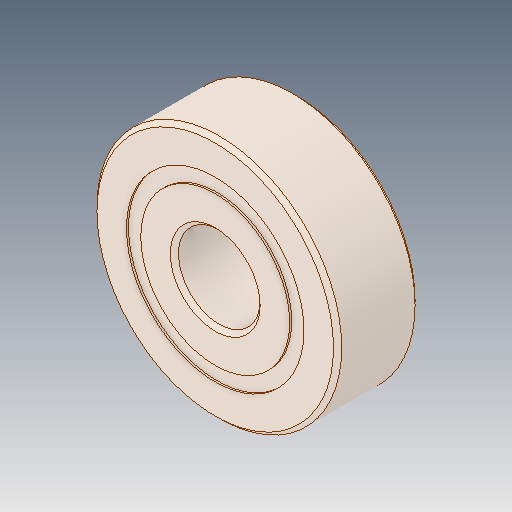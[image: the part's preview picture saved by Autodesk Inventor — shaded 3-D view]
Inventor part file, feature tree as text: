
AUTODESK INVENTOR PART (.ipt)
format: ipt  version: 2019 (Build 230136000, 136)  size: 607,232 bytes
history: native  units: mm
features: other x11, revolve x5
ambient origin geometry x8: Origin, YZ Plane, XZ Plane, XY Plane, X Axis, Y Axis, Z Axis, Center Point
bodies: Solid1 (feature_tree), Solid2 (feature_tree), Solid3 (feature_tree), Solid4 (feature_tree), Solid5 (feature_tree), Solid6 (feature_tree), Solid7 (feature_tree), Solid8 (feature_tree), Solid9 (feature_tree), Solid10 (feature_tree), Solid11 (feature_tree), Solid12 (feature_tree), Solid13 (feature_tree), Solid14 (feature_tree), Solid15 (feature_tree), Solid16 (feature_tree)
feature tree (16):
  revolve  "Revolve1"  [1 undecoded]
  revolve  "Revolve3"  [1 undecoded]
  revolve  "Revolve4"  [1 undecoded]
  other  "CirPattern1[1]"
  other  "CirPattern1[2]"
  other  "CirPattern1[3]"
  other  "CirPattern1[4]"
  other  "CirPattern1[5]"
  other  "CirPattern1[6]"
  other  "CirPattern1[7]"
  other  "CirPattern1[8]"
  other  "CirPattern1[9]"
  other  "CirPattern1[10]"
  other  "CirPattern1[11]"
  revolve  "Revolve5[1]"  [1 undecoded]
  revolve  "Revolve5[2]"  [1 undecoded]
note: 5 required parameter values undecoded (feature->parameter linkage not recoverable at this tier; creation-order binding heuristic only, values carry confidence <= 0.55)
